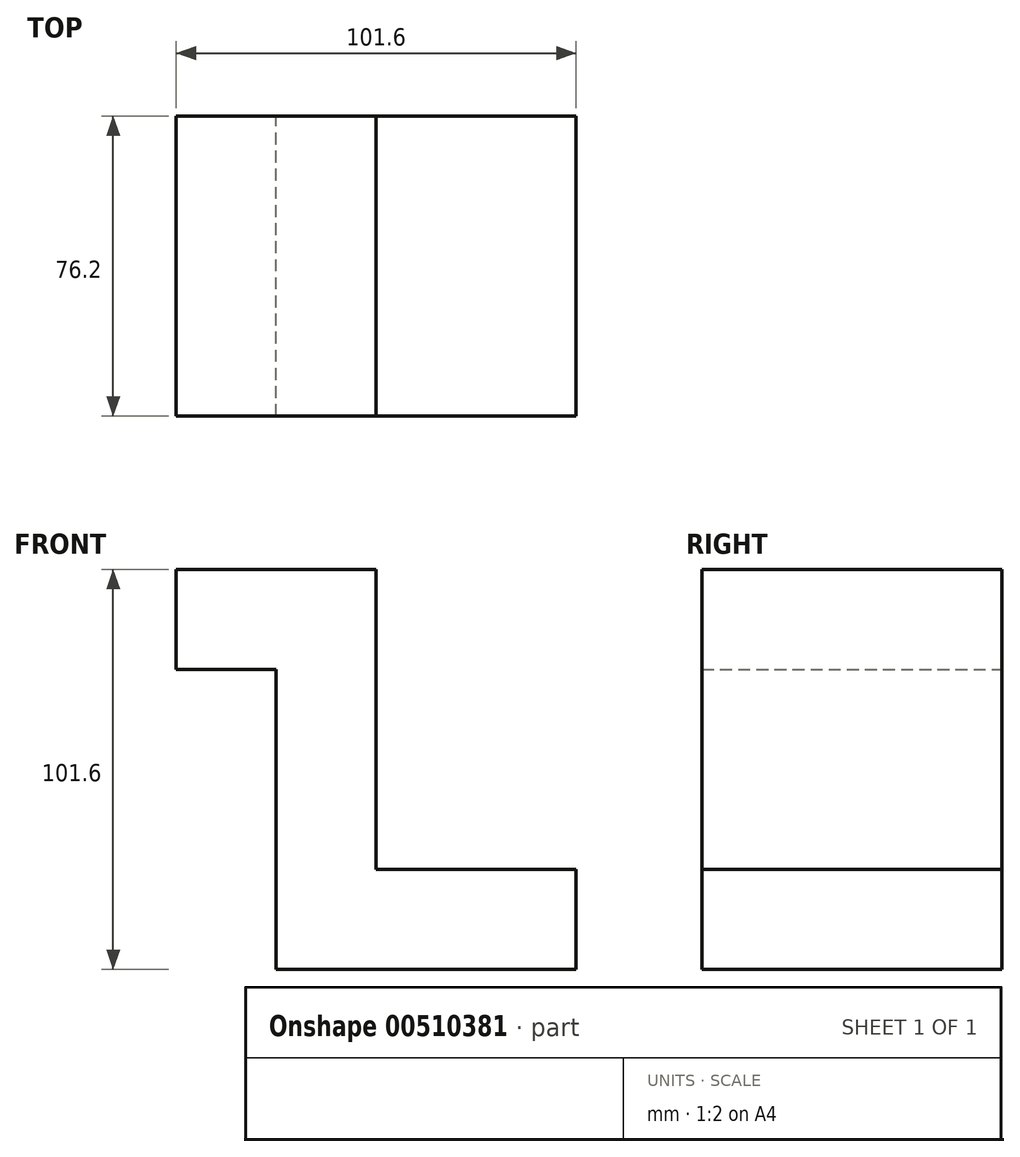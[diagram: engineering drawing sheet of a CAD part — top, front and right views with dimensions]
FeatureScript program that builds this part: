
annotation { "Feature Type Name" : "Feature", "Feature Type Description" : "" }
export const myFeature = defineFeature(function(context is Context, id is Id, definition is map)
    precondition{}
    {
        {
            var Q0;
            Q0=qCreatedBy(makeId("Front.planeOp"),FACE);
            var sketch = newSketch(context, id + "F0", { "sketchPlane" : qUnion([Q0])});
            skLineSegment(sketch, "E0", {"start": v(-74.56, 67.19) * mm, "end": v(-74.56, 41.79) * mm});
            skLineSegment(sketch, "E1", {"start": v(-74.56, 41.79) * mm, "end": v(-49.16, 41.79) * mm});
            skLineSegment(sketch, "E2", {"start": v(-49.16, 41.79) * mm, "end": v(-49.16, -34.41) * mm});
            skLineSegment(sketch, "E3", {"start": v(-49.16, -34.41) * mm, "end": v(27.04, -34.41) * mm});
            skLineSegment(sketch, "E4", {"start": v(27.04, -34.41) * mm, "end": v(27.04, -9.01) * mm});
            skLineSegment(sketch, "E5", {"start": v(27.04, -9.01) * mm, "end": v(-23.76, -9.01) * mm});
            skLineSegment(sketch, "E6", {"start": v(-23.76, -9.01) * mm, "end": v(-23.76, 67.19) * mm});
            skLineSegment(sketch, "E7", {"start": v(-23.76, 67.19) * mm, "end": v(-74.56, 67.19) * mm});
            skSolve(sketch);
        }
        {
            var Q0;
            Q0=makeQuery(id+"F0.imprint","IMPRINT",FACE,{"disambiguationData":[TD([[makeQuery(id+"F0.imprint","IMPRINT",EDGE,{"derivedFrom":sQuery(id+"F0.wireOp",EDGE,"E0")}),1.0]])]});
            extrude(context, id + "F1", {"entities" : qUnion([Q0]), "depth" : 25.4 * mm});
        }
        {
            var Q0;
            Q0=makeQuery(id+"F1.opExtrude","CAP_FACE",FACE,{"disambiguationData":[OSD([sQuery(id+"F0.wireOp",EDGE,"E0"),sQuery(id+"F0.wireOp",EDGE,"E1"),sQuery(id+"F0.wireOp",EDGE,"E2"),sQuery(id+"F0.wireOp",EDGE,"E3"),sQuery(id+"F0.wireOp",EDGE,"E4"),sQuery(id+"F0.wireOp",EDGE,"E5"),sQuery(id+"F0.wireOp",EDGE,"E6"),sQuery(id+"F0.wireOp",EDGE,"E7")])],"isStart":false});
            extrude(context, id + "F2", {"entities" : qUnion([Q0]), "operationType" : NewBodyOperationType.ADD, "depth" : 25.4 * mm});
        }
        {
            var Q0;
            Q0=makeQuery(id+"F2.opExtrude","CAP_FACE",FACE,{"disambiguationData":[OSD([sQuery(id+"F0.wireOp",EDGE,"E0"),sQuery(id+"F0.wireOp",EDGE,"E1"),sQuery(id+"F0.wireOp",EDGE,"E2"),sQuery(id+"F0.wireOp",EDGE,"E3"),sQuery(id+"F0.wireOp",EDGE,"E4"),sQuery(id+"F0.wireOp",EDGE,"E5"),sQuery(id+"F0.wireOp",EDGE,"E6"),sQuery(id+"F0.wireOp",EDGE,"E7")])],"isStart":false});
            extrude(context, id + "F3", {"entities" : qUnion([Q0]), "operationType" : NewBodyOperationType.ADD, "depth" : 25.4 * mm});
        }
    });
